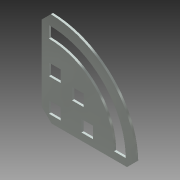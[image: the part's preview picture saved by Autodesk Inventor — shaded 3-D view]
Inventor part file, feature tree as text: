
AUTODESK INVENTOR PART (.ipt)
format: ipt  version: 2013 (Build 170138000, 138)  size: 164,864 bytes
history: native  units: mm (DEFAULTED — no unit token found)
features: extrude x7, other x6, sketch x5, pattern_linear x2
ambient origin geometry x8: Origin, YZ Plane, XZ Plane, XY Plane, X Axis, Y Axis, Z Axis, Center Point
bodies: Solid1 (feature_tree)
feature tree (20):
  extrude  "Extrusion1"  Depth=4.572mm
  pattern_linear  "Rectangular Pattern1"  Spacing1=8.128mm  [1 undecoded]
  pattern_linear  "Rectangular Pattern2"  Spacing1=8.128mm  [1 undecoded]
  sketch  "Sketch1"  dims[d0=4.572mm d1=4.572mm]
  sketch  "Sketch2"  dims[d2=4.572mm]
  other  "Srf1"
  other  "Srf2"
  other  "Srf3"
  sketch  "Sketch3"  dims[d3=4.572mm]
  other  "Srf4"
  sketch  "Sketch4"  dims[d4=4.572mm]
  other  "Srf5"
  sketch  "Sketch5"  dims[d5=4.572mm d6=8.128mm d8=8.128mm d10=4.064mm d11=2.794mm d12=2.794mm d13=3.81mm d14=3.81mm d15=3.81mm d16=3.81mm d18=45.0deg d22=4.572mm d23=4.445mm d24=4.445mm d25=4.572mm d26=0.8382mm d27=0.0mm d28=25.4mm d29=0.0mm d30=20.0mm d32=12.7mm d33=20.0mm d35=12.7mm d36=25.4mm d37=0.0mm d38=0.0mm d39=0.0mm d40=0.0mm d41=0.0mm d42=0.0mm d43=0.0mm d44=0.0mm d45=0.0mm d46=25.4mm d47=0.0mm d48=25.4mm d49=0.0mm d50=0.0mm d51=0.0mm d52=0.0mm d53=0.0mm]
  other  "Srf6"
  extrude  "ExtrusionSrf1"  Depth=4.064mm
  extrude  "ExtrusionSrf4"  Depth=2.794mm
  extrude  "ExtrusionSrf5"  Depth=2.794mm
  extrude  "ExtrusionSrf6"  Depth=3.81mm
  extrude  "ExtrusionSrf2"  Depth=3.81mm
  extrude  "ExtrusionSrf3"  Depth=3.81mm
note: 2 required parameter values undecoded (feature->parameter linkage not recoverable at this tier; creation-order binding heuristic only, values carry confidence <= 0.55)
